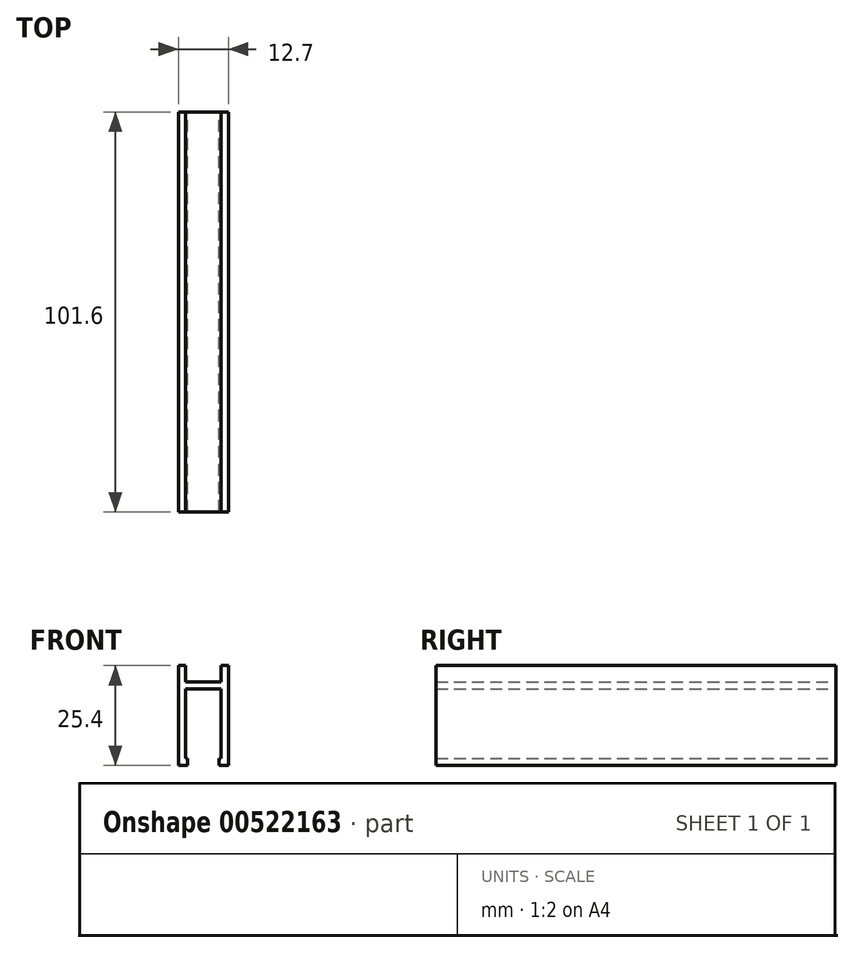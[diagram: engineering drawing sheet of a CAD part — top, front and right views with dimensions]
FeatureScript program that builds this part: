
annotation { "Feature Type Name" : "Feature", "Feature Type Description" : "" }
export const myFeature = defineFeature(function(context is Context, id is Id, definition is map)
    precondition{}
    {
        {
            var Q0;
            Q0=qCreatedBy(makeId("Front.planeOp"),FACE);
            var sketch = newSketch(context, id + "F0", { "sketchPlane" : qUnion([Q0])});
            skLineSegment(sketch, "E0", {"start": v(0, 21.2) * mm, "end": v(4.57, 21.2) * mm});
            skLineSegment(sketch, "E1", {"start": v(4.57, 21.2) * mm, "end": v(4.57, 25.4) * mm});
            skLineSegment(sketch, "E2", {"start": v(4.57, 25.4) * mm, "end": v(6.35, 25.4) * mm});
            skLineSegment(sketch, "E3", {"start": v(6.35, 25.4) * mm, "end": v(6.35, 0) * mm});
            skLineSegment(sketch, "E4", {"start": v(6.35, 0) * mm, "end": v(3.99, 0) * mm});
            skLineSegment(sketch, "E5", {"start": v(3.99, 0) * mm, "end": v(3.99, 1.78) * mm});
            skLineSegment(sketch, "E6", {"start": v(3.99, 1.78) * mm, "end": v(4.57, 1.78) * mm});
            skLineSegment(sketch, "E7", {"start": v(4.57, 1.78) * mm, "end": v(4.57, 19.43) * mm});
            skLineSegment(sketch, "E8", {"start": v(4.57, 19.43) * mm, "end": v(0, 19.43) * mm});
            skLineSegment(sketch, "E9.MirrorCS", {"start": v(-3.99, 1.78) * mm, "end": v(-4.57, 1.78) * mm});
            skLineSegment(sketch, "E10.MirrorCS", {"start": v(-4.57, 19.43) * mm, "end": v(0, 19.43) * mm});
            skLineSegment(sketch, "E11.MirrorCS", {"start": v(-4.57, 1.78) * mm, "end": v(-4.57, 19.43) * mm});
            skLineSegment(sketch, "E12.MirrorCS", {"start": v(-4.57, 21.2) * mm, "end": v(-4.57, 25.4) * mm});
            skLineSegment(sketch, "E13.MirrorCS", {"start": v(0, 21.2) * mm, "end": v(-4.57, 21.2) * mm});
            skLineSegment(sketch, "E14.MirrorCS", {"start": v(-6.35, 0) * mm, "end": v(-3.99, 0) * mm});
            skLineSegment(sketch, "E15.MirrorCS", {"start": v(-6.35, 25.4) * mm, "end": v(-6.35, 0) * mm});
            skLineSegment(sketch, "E16.MirrorCS", {"start": v(-4.57, 25.4) * mm, "end": v(-6.35, 25.4) * mm});
            skLineSegment(sketch, "E17.MirrorCS", {"start": v(-3.99, 0) * mm, "end": v(-3.99, 1.78) * mm});
            skSolve(sketch);
        }
        {
            var Q0;
            Q0 = qSketchRegion(id + "F0", true);
            extrude(context, id + "F1", {"entities" : qUnion([Q0]), "depth" : 101.6 * mm, "offsetDistance" : 25.4 * mm});
        }
    });
